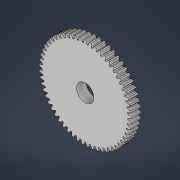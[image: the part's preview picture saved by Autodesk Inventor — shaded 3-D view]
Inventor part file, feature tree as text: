
AUTODESK INVENTOR PART (.ipt)
format: ipt  version: 2021 (Build 250183000, 183)  size: 405,504 bytes
history: native  units: mm (DEFAULTED — no unit token found)
features: plane x3, other x3, sketch x3, extrude x2
ambient origin geometry x8: Origin, YZ Plane, XZ Plane, XY Plane, X Axis, Y Axis, Z Axis, Center Point
bodies: Solid1 (feature_tree)
feature tree (11):
  extrude  "Extrusion1"  Depth=0.5mm TaperAngle=0.0deg
  plane  "Work Plane2"
  plane  "Work Plane8"
  plane  "Work Plane9"
  other  "Engrenagem reta"
  extrude  "Extrusão2"  Depth=10.0mm TaperAngle=0.0deg
  sketch  "Sketch1"  dims[d0=4.776mm d1=0.5mm d2=0.0mm]
  sketch  "Sketch2"  dims[d3=4.56mm d4=10.0mm d5=0.0mm]
  other  "Srf1"
  sketch  "Esboço3"  dims[d16=3.188mm d17=0.0mm d34=0.551157mm d39=0.0mm d41=0.0mm d43=3.188mm d46=3.188mm d47=0.0mm d48=0.0mm d49=0.9mm d50=0.5mm d51=0.0mm]
  other  "Diâmetro do flanco"
